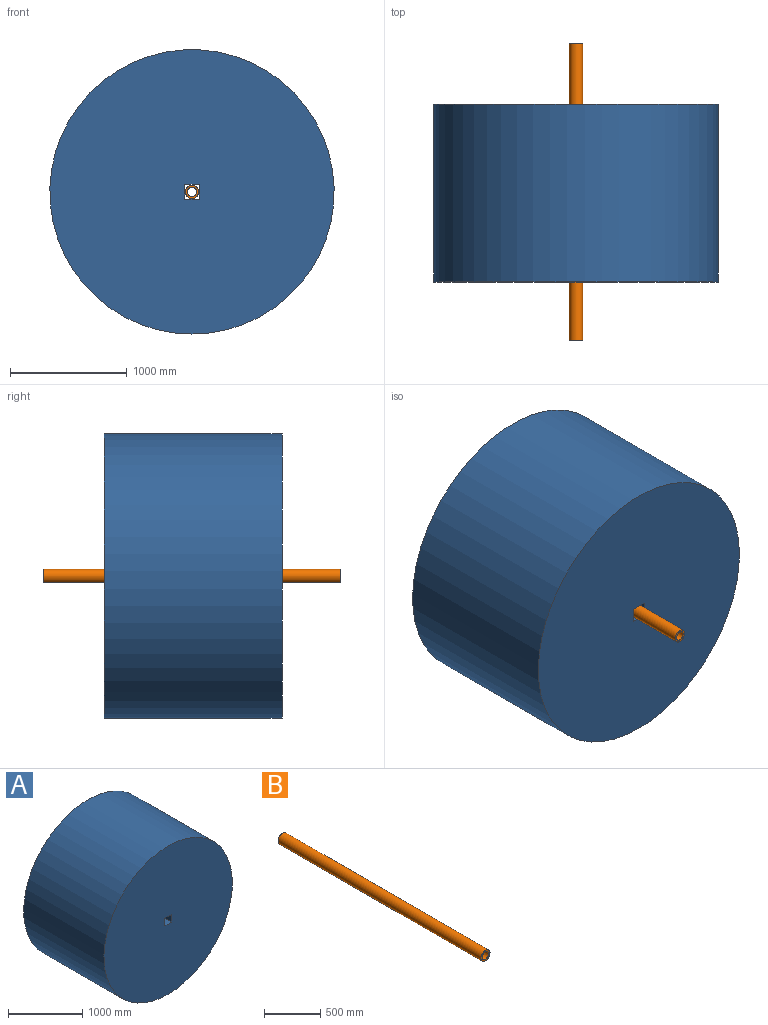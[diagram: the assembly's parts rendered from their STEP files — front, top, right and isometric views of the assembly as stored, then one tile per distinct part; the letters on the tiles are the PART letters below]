
ASSEMBLY  parts=2 mates=1
PART A: 7 faces, bbox 2438.4x1524x2438.4 mm
  f0: plane 1524x127mm, normal (0,0,-1), area 193548mm2, adj f1,f4,f5,f6
  f1: plane 1524x127mm, normal (-1,0,0), area 193548mm2, adj f0,f2,f5,f6
  f2: plane 1524x127mm, normal (0,0,1), area 193548mm2, adj f1,f4,f5,f6
  f3: cylinder r=1219.2mm len=2438.4mm, axis (0,1,0), area 11674540.3mm2, adj f5,f6
  f4: plane 1524x127mm, normal (1,0,0), area 193548mm2, adj f0,f2,f5,f6
  f5: plane 2438.4x2438.4mm, normal (0,-1,0), area 4653687.1mm2, adj f0,f1,f2,f3,f4
  f6: plane 2438.4x2438.4mm, normal (0,1,0), area 4653687.1mm2, adj f0,f1,f2,f3,f4
PART B: 4 faces, bbox 114.3x2540x114.3 mm
  f0: cylinder r=40.03mm len=2540mm, axis (0,1,0), area 638856.8mm2, adj f2,f3
  f1: cylinder r=57.15mm len=2540mm, axis (0,1,0), area 912073.5mm2, adj f2,f3
  f2: plane 114.3x114.3mm, normal (0,-1,0), area 5226.6mm2, adj f0,f1
  f3: plane 114.3x114.3mm, normal (0,1,0), area 5226.6mm2, adj f0,f1
PLACE A t=(1334.91,449.97,83.77)mm
PLACE B t=(1334.91,968.13,83.77)mm
MATE cylindrical B.f1 <-> A.f3  axis (0,1,0) through (1334.91,-301.87,83.77)mm
